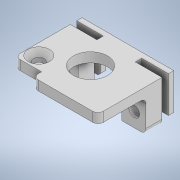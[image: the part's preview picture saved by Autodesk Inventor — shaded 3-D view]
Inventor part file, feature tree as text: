
AUTODESK INVENTOR PART (.ipt)
format: ipt  version: 2021 (Build 250183000, 183)  size: 268,288 bytes
history: native  units: mm
features: sketch x12, extrude x10, fillet x3, hole x2, chamfer x1
ambient origin geometry x8: Origin, YZ Plane, XZ Plane, XY Plane, X Axis, Y Axis, Z Axis, Center Point
bodies: Solid1 (feature_tree)
feature tree (28):
  extrude  "Extrusion1"  Depth=7.2mm
  extrude  "Extrusion2"  Depth=5.0mm
  extrude  "Extrusion3"  Depth=12.0mm TaperAngle=0.0deg
  extrude  "Extrusion4"  Depth=1.0mm TaperAngle=0.0deg
  hole  "Hole1"  [1 undecoded]
  extrude  "Extrusion5"  Depth=3.0mm
  extrude  "Extrusion6"  Depth=5.0mm TaperAngle=0.0deg
  extrude  "Extrusion7"  Depth=7.0mm
  extrude  "Extrusion8"  Depth=5.0mm TaperAngle=0.0deg
  fillet  "Fillet1"  Radius=1.6mm
  fillet  "Fillet2"  Radius=5.0mm
  extrude  "Extrusion9"  Depth=1.0mm
  fillet  "Fillet4"  Radius=1.0mm
  chamfer  "Chamfer3"  Distance=1.0mm
  extrude  "Extrusion10"  Depth=1.0mm
  hole  "Hole2"  [1 undecoded]
  sketch  "Sketch1"  dims[d0=7.2mm d1=2.0mm]
  sketch  "Sketch2"  dims[d2=8.0mm d3=5.0mm]
  sketch  "Sketch3"  dims[d4=5.0mm d5=12.0mm d6=0.0mm]
  sketch  "Sketch4"  dims[d7=1.2mm d8=0.0mm d9=1.0mm d10=0.0mm]
  sketch  "Sketch5"  dims[d11=9.0mm d12=0.0mm d13=5.3mm]
  sketch  "Sketch6"  dims[d14=3.0mm d15=5.3mm]
  sketch  "Sketch7"  dims[d16=2.8mm]
  sketch  "Sketch8"  dims[d17=2.0mm d18=6.0mm d19=4.0mm d20=2.0mm d21=90.0deg d22=5.0mm d23=20.594885mm d24=2.0mm d25=0.0mm]
  sketch  "Sketch9"  dims[d29=0.2mm d30=0.0mm d31=7.0mm]
  sketch  "Sketch10"  dims[d32=6.4mm d33=2.0mm d34=0.0mm d35=1.6mm d36=5.0mm]
  sketch  "Sketch11"  dims[d37=2.0mm d38=0.0mm d39=1.0mm d40=1.0mm]
  sketch  "Sketch12"  dims[d45=1.0mm d46=1.0mm d47=0.0mm d48=1.0mm d49=1.0mm d50=2.0mm d51=45.0deg d52=8.2mm d53=0.5mm d54=0.5mm d55=10.0mm d56=0.0mm d57=2.1mm d58=2.4mm d59=2.0mm d60=6.0mm d61=4.0mm d62=2.0mm d63=90.0deg d64=5.0mm d65=20.594885mm]
note: 2 required parameter values undecoded (feature->parameter linkage not recoverable at this tier; creation-order binding heuristic only, values carry confidence <= 0.55)
